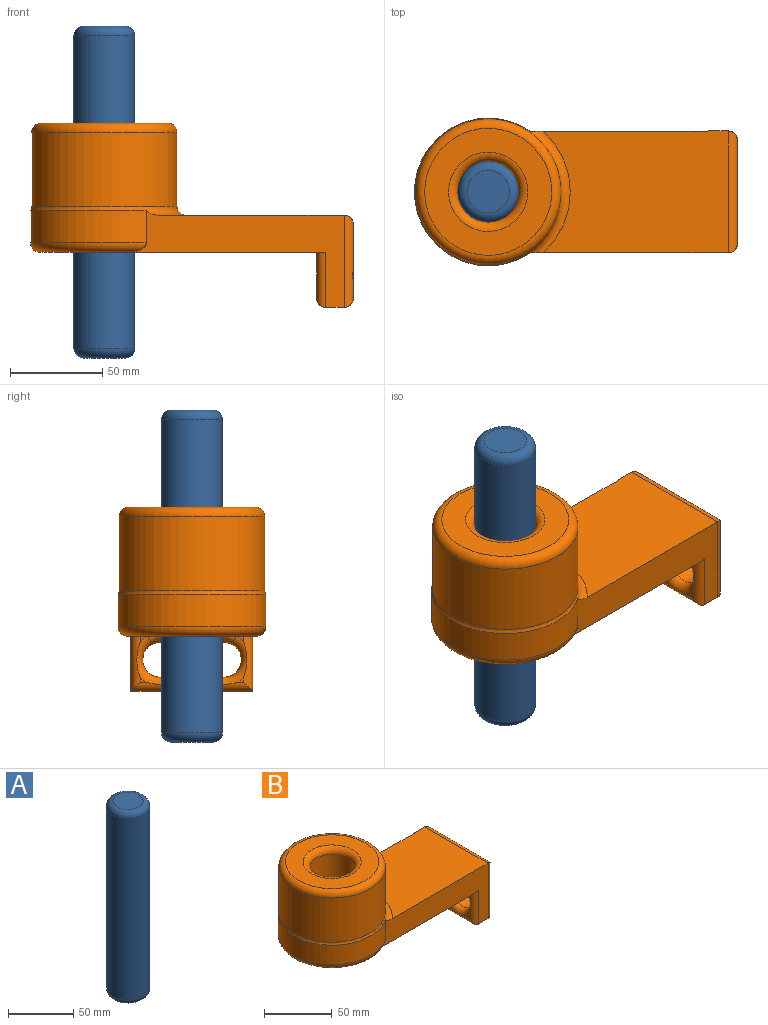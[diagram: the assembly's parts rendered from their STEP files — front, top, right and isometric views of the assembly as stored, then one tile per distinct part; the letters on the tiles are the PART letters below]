
ASSEMBLY  parts=2 mates=1
PART A: 5 faces, bbox 35.7x35.7x180 mm
  f0: cylinder r=16.5mm len=170mm, axis (0,0,-1), area 17624.3mm2, adj f3,f4
  f1: plane 23x23mm, normal (0,0,1), area 415.5mm2, adj f4
  f2: plane 23x23mm, normal (0,0,-1), area 415.5mm2, adj f3
  f3: torus R=11.5mm, axis (0,0,1), area 724.6mm2, adj f0,f2
  f4: torus R=11.5mm, axis (0,0,1), area 724.6mm2, adj f0,f1
PART B: 37 faces, bbox 187.4x104.2x102.7 mm
  f0: plane 3.06x2.63mm, normal (1,0,0), area 3.6mm2, adj f30,f31,f32
  f1: plane 2.85x2.4mm, normal (1,0,0), area 3.1mm2, adj f27,f28,f30
  f2: plane 4.18x3.29mm, normal (-1,0,0), area 6mm2, adj f7,f24,f25
  f3: plane 3.06x2.63mm, normal (-1,0,0), area 3.6mm2, adj f23,f24,f25
  f4: plane 3.97x3.05mm, normal (-1,0,0), area 5.3mm2, adj f7,f21,f22
  f5: plane 2.85x2.4mm, normal (-1,0,0), area 3.1mm2, adj f21,f22,f23
  f6: plane 107.04x23.01mm, normal (0,1,0), area 1933.7mm2, adj f7,f8,f12,f24,f33,f36
  f7: plane 155.29x70.2mm, normal (0,0,-1), area 8684mm2, adj f2,f4,f6,f9,f11,f19,f20,f22
  f8: cylinder r=40mm len=80mm, axis (0,0,1), area 3075.1mm2, adj f6,f9,f33,f36
  f9: plane 118.48x53.02mm, normal (0,-1,0), area 2462.4mm2, adj f7,f8,f12,f15,f22,f27,f33,f36
  f10: plane 56x40mm, normal (1,0,0), area 1063.8mm2, adj f27,f28,f29,f30,f31,f32
  f11: cylinder r=16.5mm len=65mm, axis (0,0,1), area 6738.7mm2, adj f7,f34
  f12: plane 100.23x66mm, normal (0,0,1), area 5933.2mm2, adj f6,f9,f17,f24,f29,f33
  f13: cylinder r=39.42mm len=78.84mm, axis (0,0,-1), area 9907.6mm2, adj f33,f35
  f14: plane 68.84x68.84mm, normal (0,0,1), area 2270mm2, adj f34,f35
  f15: plane 66x10mm, normal (0,0,-1), area 660mm2, adj f9,f17,f23,f30
  f16: cylinder r=9.47mm len=18.95mm, axis (1,0,0), area 595.2mm2, adj f25,f26,f32
  f17: plane 50x10mm, normal (0,1,0), area 500mm2, adj f12,f15,f24,f31
  f18: cylinder r=9.47mm len=18.95mm, axis (1,0,0), area 595.2mm2, adj f20,f21,f28
  f19: plane 25x21.03mm, normal (-1,0,0), area 242.2mm2, adj f7,f21,f23,f25
  f20: bspline ~15.02x5.52mm, area 70.4mm2, adj f7,f18,f21
  f21: torus R=14.47mm, axis (1,0,0), area 432.6mm2, adj f4,f5,f18,f19,f20,f22,f23
  f22: cylinder r=5mm len=30mm, axis (0,0,-1), area 196.2mm2, adj f4,f5,f7,f9,f21,f23
  f23: cylinder r=5mm len=66mm, axis (0,-1,0), area 465.7mm2, adj f3,f5,f15,f19,f21,f22,f24,f25
  f24: cylinder r=5mm len=50mm, axis (0,0,-1), area 227.3mm2, adj f2,f3,f6,f7,f12,f17,f23,f25
  f25: torus R=14.47mm, axis (1,0,0), area 434.8mm2, adj f2,f3,f16,f19,f23,f24,f26
  f26: bspline ~15.02x5.52mm, area 70.4mm2, adj f7,f16,f25
  f27: cylinder r=5mm len=50mm, axis (0,0,-1), area 345.1mm2, adj f1,f9,f10,f28,f29,f30
  f28: torus R=14.47mm, axis (-1,0,0), area 524.7mm2, adj f1,f10,f18,f27,f30
  f29: cylinder r=5mm len=66mm, axis (0,1,0), area 489.8mm2, adj f10,f12,f27,f31
  f30: cylinder r=5mm len=66mm, axis (0,-1,0), area 465.7mm2, adj f0,f1,f10,f15,f27,f28,f31,f32
  f31: cylinder r=5mm len=50mm, axis (0,0,-1), area 341mm2, adj f0,f10,f17,f29,f30,f32
  f32: torus R=14.47mm, axis (-1,0,0), area 520.2mm2, adj f0,f10,f16,f30,f31
  f33: torus R=44.42mm, axis (0,0,1), area 1013.9mm2, adj f6,f8,f9,f12,f13
  f34: torus R=21.5mm, axis (0,0,1), area 903.9mm2, adj f11,f14
  f35: torus R=34.42mm, axis (0,0,1), area 1855.7mm2, adj f13,f14
  f36: torus R=35mm, axis (0,0,1), area 1258.8mm2, adj f6,f7,f8,f9
PLACE A t=(-179.51,-78.18,43.06)mm
PLACE B t=(-96.97,-78.18,30.47)mm
MATE slider A.f0 <-> B.f8  axis (0,0,-1) through (-179.51,-78.18,43.06)mm
